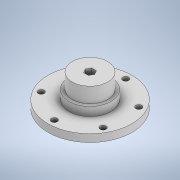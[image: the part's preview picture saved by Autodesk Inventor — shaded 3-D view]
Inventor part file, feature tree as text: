
AUTODESK INVENTOR PART (.ipt)
format: ipt  version: 2020.2 (Build 242310000, 310)  size: 146,944 bytes
history: native  units: in
note: dims shown in document units (in); Inventor stores cm internally (conversion verified against a paired STEP export)
features: extrude x5, sketch x5
ambient origin geometry x8: Origin, YZ Plane, XZ Plane, XY Plane, X Axis, Y Axis, Z Axis, Center Point
bodies: Solid1 (feature_tree)
feature tree (10):
  extrude  "Extrusion1"  Depth=0.2in TaperAngle=0.0deg
  extrude  "Extrusion2"  Depth=0.23in TaperAngle=0.0deg
  extrude  "Extrusion3"  Depth=0.4in TaperAngle=0.0deg
  extrude  "Extrusion4"  Depth=1.0in TaperAngle=0.0deg
  extrude  "Extrusion5"  Depth=0.0344in
  sketch  "Sketch1"  dims[d0=2.2in d1=0.2in d2=0.0in]
  sketch  "Sketch2"  dims[d3=1.1in d4=0.23in d5=0.0in]
  sketch  "Sketch3"  dims[d6=0.93in d7=0.4in d8=0.0in]
  sketch  "Sketch5"  dims[d10=0.105in d11=1.0in d12=0.0in]
  sketch  "Sketch6"  dims[d15=1.0in d16=0.0in d13=0.0344in]
